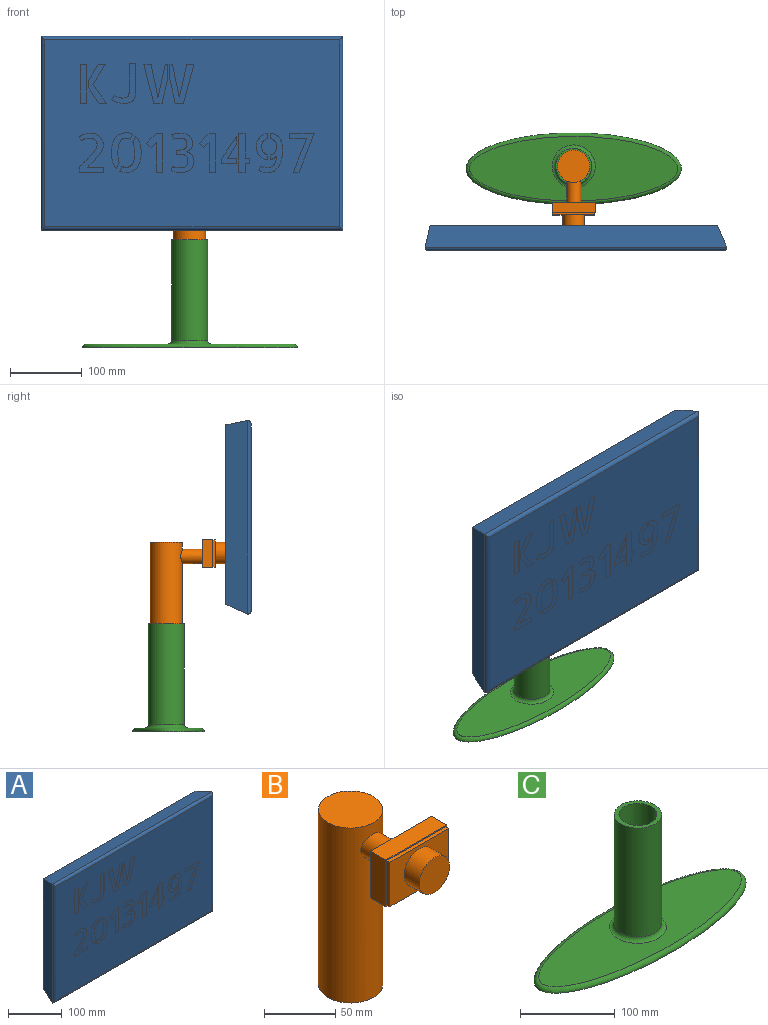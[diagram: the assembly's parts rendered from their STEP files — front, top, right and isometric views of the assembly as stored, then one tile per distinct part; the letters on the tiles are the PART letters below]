
ASSEMBLY  parts=3 mates=3
PART A: 285 faces, bbox 420x35.1x270 mm
  f0: plane 170x100mm, normal (0,1,0), area 13619.9mm2, adj f11,f12,f13,f14,f15,f16,f17,f18
  f1: plane 410x260mm, normal (0,-1,0), area 97142mm2, adj f7,f8,f9,f10,f33,f34,f35,f36
  f2: plane 400x250mm, normal (0,1,0), area 82293.1mm2, adj f3,f4,f5,f6,f11,f12,f13,f14
  f3: plane 270x30mm, normal (-0.98,0.22,0), area 7998.6mm2, adj f2,f4,f6,f7
  f4: plane 420x30mm, normal (0,0.42,-0.91), area 13536.7mm2, adj f2,f3,f5,f9
  f5: plane 270x30mm, normal (0.92,0.4,0), area 8520.4mm2, adj f2,f4,f6,f10
  f6: plane 420x30mm, normal (0,0.2,0.98), area 12561mm2, adj f2,f3,f5,f8
  f7: cylinder r=5mm len=270mm, axis (0,0,-1), area 2092mm2, adj f1,f3,f8,f9
  f8: cylinder r=5mm len=420mm, axis (-1,0,0), area 3270.1mm2, adj f1,f6,f7,f10
  f9: cylinder r=5mm len=420mm, axis (1,0,0), area 3270.1mm2, adj f1,f4,f7,f10
  f10: cylinder r=5mm len=270mm, axis (0,0,1), area 2092mm2, adj f1,f5,f8,f9
  f11: plane 100x15mm, normal (-1,0,0), area 1500mm2, adj f0,f2,f12,f14
  f12: plane 170x15mm, normal (0,0,1), area 2550mm2, adj f0,f2,f11,f13
  f13: plane 100x15mm, normal (1,0,0), area 1500mm2, adj f0,f2,f12,f14
  f14: plane 170x15mm, normal (0,0,-1), area 2550mm2, adj f0,f2,f11,f13
  f15: plane 15x10mm, normal (-1,0,0), area 150mm2, adj f0,f16,f18,f19
  f16: plane 30x10mm, normal (0,0,1), area 300mm2, adj f0,f15,f17,f19
  f17: plane 15x10mm, normal (1,0,0), area 150mm2, adj f0,f16,f18,f19
  f18: plane 30x10mm, normal (0,0,-1), area 300mm2, adj f0,f15,f17,f19
  f19: plane 30x15mm, normal (0,1,0), area 450mm2, adj f15,f16,f17,f18
  f20: plane 60x15mm, normal (0,0,1), area 900mm2, adj f0,f21,f23,f24
  f21: plane 40x15mm, normal (1,0,0), area 600mm2, adj f0,f20,f22,f24
  f22: plane 60x15mm, normal (0,0,-1), area 900mm2, adj f0,f21,f23,f24
  f23: plane 40x15mm, normal (-1,0,0), area 600mm2, adj f0,f20,f22,f24
  f24: plane 60x40mm, normal (0,1,0), area 2400mm2, adj f20,f21,f22,f23
  f25: cylinder r=7.5mm len=15mm, axis (0,1,0), area 706.9mm2, adj f0,f26
  f26: plane 15x15mm, normal (0,1,0), area 176.7mm2, adj f25
  f27: cylinder r=7.5mm len=15mm, axis (0,1,0), area 706.9mm2, adj f0,f28
  f28: plane 15x15mm, normal (0,1,0), area 176.7mm2, adj f27
  f29: cylinder r=7.5mm len=15mm, axis (0,1,0), area 706.9mm2, adj f0,f30
  f30: plane 15x15mm, normal (0,1,0), area 176.7mm2, adj f29
  f31: cylinder r=15mm len=30mm, axis (0,1,0), area 942.5mm2, adj f2,f32
  f32: plane 30x30mm, normal (0,1,0), area 706.9mm2, adj f31
  f33: plane 8.95x0.1mm, normal (0,0,-1), area 0.9mm2, adj f1,f34,f36,f37
  f34: plane 54.03x0.1mm, normal (1,0,0), area 5.4mm2, adj f1,f33,f35,f37
  f35: plane 8.95x0.1mm, normal (0,0,1), area 0.9mm2, adj f1,f34,f36,f37
  f36: plane 54.03x0.1mm, normal (-1,0,0), area 5.4mm2, adj f1,f33,f35,f37
  f37: plane 54.03x8.95mm, normal (0,-1,0), area 483.5mm2, adj f33,f34,f35,f36
  f38: plane 27.78x17.3mm, normal (0.85,0,-0.53), area 3.3mm2, adj f1,f39,f44,f45
  f39: plane 10.04x0.1mm, normal (0,0,1), area 1mm2, adj f1,f38,f40,f45
  f40: plane 22.06x13.13mm, normal (-0.86,0,0.51), area 2.6mm2, adj f1,f39,f41,f45
  f41: plane 10.7x0.1mm, normal (-1,0,0), area 1.1mm2, adj f1,f40,f42,f45
  f42: plane 21.27x14.44mm, normal (-0.83,0,-0.56), area 2.6mm2, adj f1,f41,f43,f45
  f43: plane 10.19x0.1mm, normal (0,0,-1), area 1mm2, adj f1,f42,f44,f45
  f44: plane 26.25x18.77mm, normal (0.81,0,0.58), area 3.2mm2, adj f1,f38,f43,f45
  f45: plane 54.03x24.63mm, normal (0,-1,0), area 505.1mm2, adj f38,f39,f40,f41,f42,f43,f44
  f46: plane 8.94x0.1mm, normal (0,0,1), area 0.9mm2, adj f1,f47,f63,f64
  f47: plane 41.35x0.1mm, normal (-1,0,0), area 4.1mm2, adj f1,f46,f48,f64
  f48: extruded ~5.09x2.46mm, area 0.6mm2, adj f1,f47,f49,f64
  f49: extruded ~6.2x1.5mm, area 0.6mm2, adj f1,f48,f50,f64
  f50: extruded ~3.3x0.36mm, area 0.3mm2, adj f1,f49,f51,f64
  f51: extruded ~3.37x0.84mm, area 0.3mm2, adj f1,f50,f52,f64
  f52: extruded ~2.97x1.03mm, area 0.3mm2, adj f1,f51,f53,f64
  f53: extruded ~2.09x1.07mm, area 0.2mm2, adj f1,f52,f54,f64
  f54: plane 5.94x3.73mm, normal (-0.85,0,0.53), area 0.7mm2, adj f1,f53,f55,f64
  f55: extruded ~3.59x1.98mm, area 0.4mm2, adj f1,f54,f56,f64
  f56: extruded ~4.43x1.58mm, area 0.5mm2, adj f1,f55,f57,f64
  f57: extruded ~4.47x1.03mm, area 0.5mm2, adj f1,f56,f58,f64
  f58: extruded ~3.77x0.33mm, area 0.4mm2, adj f1,f57,f59,f64
  f59: extruded ~6.27x0.62mm, area 0.6mm2, adj f1,f58,f60,f64
  f60: extruded ~5.39x2.2mm, area 0.6mm2, adj f1,f59,f61,f64
  f61: extruded ~4.18x3.74mm, area 0.6mm2, adj f1,f60,f62,f64
  f62: extruded ~6.42x1.39mm, area 0.7mm2, adj f1,f61,f63,f64
  f63: plane 42.07x0.1mm, normal (1,0,0), area 4.2mm2, adj f1,f46,f62,f64
  f64: plane 55.49x33.05mm, normal (0,-1,0), area 637.1mm2, adj f46,f47,f48,f49,f50,f51,f52,f53
  f65: plane 46.62x9.54mm, normal (0.98,0,0.2), area 4.8mm2, adj f1,f66,f72,f73
  f66: plane 9.97x0.1mm, normal (0,0,1), area 1mm2, adj f1,f65,f67,f73
  f67: plane 54.32x13.71mm, normal (-0.97,0,-0.24), area 5.6mm2, adj f1,f66,f68,f73
  f68: plane 11.51x0.1mm, normal (0,0,-1), area 1.2mm2, adj f1,f67,f69,f73
  f69: plane 34.75x8mm, normal (0.97,0,-0.22), area 3.6mm2, adj f1,f68,f70,f73
  f70: plane 19.56x0.1mm, normal (1,0,0), area 2mm2, adj f1,f69,f71,f73
  f71: plane 3.45x0.1mm, normal (0,0,1), area 0.3mm2, adj f1,f70,f72,f73
  f72: plane 46.62x10.26mm, normal (-0.98,0,0.21), area 4.8mm2, adj f1,f65,f71,f73
  f73: plane 54.32x33.22mm, normal (0,-1,0), area 831.4mm2, adj f65,f66,f67,f68,f69,f70,f71,f72
  f74: plane 46.62x10.35mm, normal (-0.98,0,0.22), area 4.8mm2, adj f1,f75,f81,f82
  f75: plane 46.62x9.52mm, normal (0.98,0,0.2), area 4.8mm2, adj f1,f74,f76,f82
  f76: plane 3.52x0.1mm, normal (0,0,1), area 0.4mm2, adj f1,f75,f77,f82
  f77: plane 20.96x0.1mm, normal (-1,0,0), area 2.1mm2, adj f1,f76,f78,f82
  f78: plane 33.36x7.33mm, normal (-0.98,0,-0.21), area 3.4mm2, adj f1,f77,f79,f82
  f79: plane 11.44x0.1mm, normal (0,0,-1), area 1.1mm2, adj f1,f78,f80,f82
  f80: plane 54.32x14.59mm, normal (0.97,0,-0.26), area 5.6mm2, adj f1,f79,f81,f82
  f81: plane 9.97x0.1mm, normal (0,0,1), area 1mm2, adj f1,f74,f80,f82
  f82: plane 54.32x33.36mm, normal (0,-1,0), area 830.2mm2, adj f74,f75,f76,f77,f78,f79,f80,f81
  f83: extruded ~5.64x1.07mm, area 0.6mm2, adj f1,f84,f115,f116
  f84: extruded ~5.31x3.27mm, area 0.6mm2, adj f1,f83,f85,f116
  f85: extruded ~5.61x3.92mm, area 0.7mm2, adj f1,f84,f86,f116
  f86: extruded ~8.17x1.54mm, area 0.8mm2, adj f1,f85,f87,f116
  f87: extruded ~3.81x0.33mm, area 0.4mm2, adj f1,f86,f88,f116
  f88: extruded ~4.14x0.92mm, area 0.4mm2, adj f1,f87,f89,f116
  f89: extruded ~4.04x1.54mm, area 0.4mm2, adj f1,f88,f90,f116
  f90: extruded ~3.26x2.12mm, area 0.4mm2, adj f1,f89,f91,f116
  f91: plane 5.43x2.57mm, normal (-0.9,0,-0.43), area 0.6mm2, adj f1,f90,f92,f116
  f92: extruded ~2.34x1.33mm, area 0.3mm2, adj f1,f91,f93,f116
  f93: extruded ~2.49x0.92mm, area 0.3mm2, adj f1,f92,f94,f116
  f94: extruded ~3.27x0.51mm, area 0.3mm2, adj f1,f93,f95,f116
  f95: extruded ~4.72x0.18mm, area 0.5mm2, adj f1,f94,f96,f116
  f96: extruded ~3.12x0.44mm, area 0.3mm2, adj f1,f95,f97,f116
  f97: extruded ~3.04x1.54mm, area 0.3mm2, adj f1,f96,f98,f116
  f98: extruded ~2.82x2.31mm, area 0.4mm2, adj f1,f97,f99,f116
  f99: extruded ~4.29x0.92mm, area 0.4mm2, adj f1,f98,f100,f116
  f100: extruded ~5.27x1.43mm, area 0.6mm2, adj f1,f99,f101,f116
  f101: extruded ~5.68x3.67mm, area 0.7mm2, adj f1,f100,f102,f116
  f102: extruded ~5.72x4.95mm, area 0.8mm2, adj f1,f101,f103,f116
  f103: extruded ~5.42x5.31mm, area 0.8mm2, adj f1,f102,f104,f116
  f104: extruded ~5.06x4.51mm, area 0.7mm2, adj f1,f103,f105,f116
  f105: extruded ~3.66x3.19mm, area 0.5mm2, adj f1,f104,f106,f116
  f106: plane 8.21x0.1mm, normal (-1,0,0), area 0.8mm2, adj f1,f105,f107,f116
  f107: plane 33.57x0.1mm, normal (0,0,-1), area 3.4mm2, adj f1,f106,f108,f116
  f108: plane 7.11x0.1mm, normal (1,0,0), area 0.7mm2, adj f1,f107,f109,f116
  f109: plane 22.94x0.1mm, normal (0,0,1), area 2.3mm2, adj f1,f108,f110,f116
  f110: extruded ~3.56x3.41mm, area 0.5mm2, adj f1,f109,f111,f116
  f111: extruded ~4.62x4.51mm, area 0.6mm2, adj f1,f110,f112,f116
  f112: extruded ~5.28x4.91mm, area 0.7mm2, adj f1,f111,f113,f116
  f113: extruded ~5.75x4.51mm, area 0.7mm2, adj f1,f112,f114,f116
  f114: extruded ~6.01x3.3mm, area 0.7mm2, adj f1,f113,f115,f116
  f115: extruded ~5.91x1.25mm, area 0.6mm2, adj f1,f83,f114,f116
  f116: plane 54.4x34.16mm, normal (0,-1,0), area 819.2mm2, adj f83,f84,f85,f86,f87,f88,f89,f90
  f117: extruded ~5.42x1.55mm, area 0.6mm2, adj f1,f118,f132,f133
  f118: plane 6.9x3.23mm, normal (0.91,0,-0.42), area 0.8mm2, adj f1,f117,f119,f133
  f119: extruded ~8.87x1.9mm, area 0.9mm2, adj f1,f118,f120,f133
  f120: extruded ~8.61x1.79mm, area 0.9mm2, adj f1,f119,f121,f133
  f121: extruded ~6.53x5.24mm, area 0.8mm2, adj f1,f120,f122,f133
  f122: extruded ~8.62x4.11mm, area 1mm2, adj f1,f121,f123,f133
  f123: extruded ~11.99x1.43mm, area 1.2mm2, adj f1,f122,f124,f133
  f124: extruded ~13.38x1.83mm, area 1.4mm2, adj f1,f123,f125,f133
  f125: extruded ~8.98x5.21mm, area 1mm2, adj f1,f124,f126,f133
  f126: plane 8.57x4.02mm, normal (0.91,0,-0.42), area 0.9mm2, adj f1,f125,f127,f133
  f127: extruded ~5.86x1.54mm, area 0.6mm2, adj f1,f126,f128,f133
  f128: extruded ~7.92x0.59mm, area 0.8mm2, adj f1,f127,f129,f133
  f129: extruded ~9.53x0.92mm, area 1mm2, adj f1,f128,f130,f133
  f130: extruded ~6.35x2.39mm, area 0.7mm2, adj f1,f129,f131,f133
  f131: extruded ~3.74x3.48mm, area 0.5mm2, adj f1,f130,f132,f133
  f132: extruded ~4.91x1.03mm, area 0.5mm2, adj f1,f117,f131,f133
  f133: plane 49.99x29.53mm, normal (0,-1,0), area 492.5mm2, adj f117,f118,f119,f120,f121,f122,f123,f124
  f134: plane 8.5x4.04mm, normal (-0.9,0,0.43), area 0.9mm2, adj f1,f135,f150,f151
  f135: extruded ~0.14x0.1mm, area 0mm2, adj f1,f134,f136,f151
  f136: extruded ~5.87x1.69mm, area 0.6mm2, adj f1,f135,f137,f151
  f137: extruded ~8.06x0.66mm, area 0.8mm2, adj f1,f136,f138,f151
  f138: extruded ~9.57x0.92mm, area 1mm2, adj f1,f137,f139,f151
  f139: extruded ~6.34x2.38mm, area 0.7mm2, adj f1,f138,f140,f151
  f140: extruded ~3.77x3.48mm, area 0.5mm2, adj f1,f139,f141,f151
  f141: extruded ~4.96x1.07mm, area 0.5mm2, adj f1,f140,f142,f151
  f142: extruded ~5.71x1.84mm, area 0.6mm2, adj f1,f141,f143,f151
  f143: plane 6.97x3.3mm, normal (-0.9,0,0.43), area 0.8mm2, adj f1,f142,f144,f151
  f144: extruded ~9.23x2.05mm, area 1mm2, adj f1,f143,f145,f151
  f145: extruded ~8.66x1.76mm, area 0.9mm2, adj f1,f144,f146,f151
  f146: extruded ~6.52x5.2mm, area 0.8mm2, adj f1,f145,f147,f151
  f147: extruded ~8.65x4.14mm, area 1mm2, adj f1,f146,f148,f151
  f148: extruded ~12.02x1.43mm, area 1.2mm2, adj f1,f147,f149,f151
  f149: extruded ~13.57x1.87mm, area 1.4mm2, adj f1,f148,f150,f151
  f150: extruded ~9.01x5.46mm, area 1.1mm2, adj f1,f134,f149,f151
  f151: plane 50.21x29.98mm, normal (0,-1,0), area 500.3mm2, adj f134,f135,f136,f137,f138,f139,f140,f141
  f152: plane 54.03x0.1mm, normal (1,0,0), area 5.4mm2, adj f1,f153,f158,f159
  f153: plane 8.95x0.1mm, normal (0,0,1), area 0.9mm2, adj f1,f152,f154,f159
  f154: plane 13.71x13.7mm, normal (-0.71,0,0.71), area 1.9mm2, adj f1,f153,f155,f159
  f155: plane 6.31x6.31mm, normal (-0.71,0,-0.71), area 0.9mm2, adj f1,f154,f156,f159
  f156: plane 7.4x7.4mm, normal (0.71,0,-0.71), area 1mm2, adj f1,f155,f157,f159
  f157: plane 41.42x0.1mm, normal (-1,0,0), area 4.1mm2, adj f1,f156,f158,f159
  f158: plane 8.95x0.1mm, normal (0,0,-1), area 0.9mm2, adj f1,f152,f157,f159
  f159: plane 54.03x22.66mm, normal (0,-1,0), area 616.6mm2, adj f152,f153,f154,f155,f156,f157,f158
  f160: plane 5.95x0.1mm, normal (-1,0,-0.01), area 0.6mm2, adj f1,f161,f204,f205
  f161: plane 7.4x0.1mm, normal (0,0,-1), area 0.7mm2, adj f1,f160,f162,f205
  f162: extruded ~6.67x2.71mm, area 0.7mm2, adj f1,f161,f163,f205
  f163: extruded ~6.67x2.28mm, area 0.7mm2, adj f1,f162,f164,f205
  f164: extruded ~6.93x2.49mm, area 0.8mm2, adj f1,f163,f165,f205
  f165: extruded ~7.56x2.75mm, area 0.8mm2, adj f1,f164,f166,f205
  f166: extruded ~5.42x0.26mm, area 0.5mm2, adj f1,f165,f167,f205
  f167: extruded ~3.08x0.66mm, area 0.3mm2, adj f1,f166,f168,f205
  f168: extruded ~1.68x0.84mm, area 0.2mm2, adj f1,f167,f169,f205
  f169: extruded ~1.26x0.8mm, area 0.1mm2, adj f1,f168,f170,f205
  f170: plane 6.3x1.97mm, normal (-0.95,0,0.3), area 0.7mm2, adj f1,f169,f171,f205
  f171: extruded ~4.94x1.72mm, area 0.5mm2, adj f1,f170,f172,f205
  f172: extruded ~9.72x0.84mm, area 1mm2, adj f1,f171,f173,f205
  f173: extruded ~2.45x0.15mm, area 0.2mm2, adj f1,f172,f174,f205
  f174: extruded ~3.48x0.66mm, area 0.4mm2, adj f1,f173,f175,f205
  f175: extruded ~3.92x1.58mm, area 0.4mm2, adj f1,f174,f176,f205
  f176: extruded ~3.63x2.83mm, area 0.5mm2, adj f1,f175,f177,f205
  f177: extruded ~4.43x2.67mm, area 0.5mm2, adj f1,f176,f178,f205
  f178: extruded ~6.33x1.06mm, area 0.6mm2, adj f1,f177,f179,f205
  f179: extruded ~5.32x1.03mm, area 0.5mm2, adj f1,f178,f180,f205
  f180: extruded ~3.92x2.56mm, area 0.5mm2, adj f1,f179,f181,f205
  f181: extruded ~3.33x2.49mm, area 0.4mm2, adj f1,f180,f182,f205
  f182: extruded ~3.48x1.1mm, area 0.4mm2, adj f1,f181,f183,f205
  f183: extruded ~2.86x1.21mm, area 0.3mm2, adj f1,f182,f184,f205
  f184: extruded ~2.79x2.31mm, area 0.4mm2, adj f1,f183,f185,f205
  f185: extruded ~3.27x2.05mm, area 0.4mm2, adj f1,f184,f186,f205
  f186: extruded ~4.13x0.81mm, area 0.4mm2, adj f1,f185,f187,f205
  f187: extruded ~6.75x1.35mm, area 0.7mm2, adj f1,f186,f188,f205
  f188: extruded ~4.69x3.67mm, area 0.6mm2, adj f1,f187,f189,f205
  f189: extruded ~5.39x2.67mm, area 0.6mm2, adj f1,f188,f190,f205
  f190: extruded ~6.53x0.84mm, area 0.7mm2, adj f1,f189,f191,f205
  f191: extruded ~7.51x0.59mm, area 0.8mm2, adj f1,f190,f192,f205
  f192: extruded ~4.36x1.09mm, area 0.4mm2, adj f1,f191,f193,f205
  f193: plane 6.6x2.56mm, normal (-0.93,0,-0.36), area 0.7mm2, adj f1,f192,f194,f205
  f194: extruded ~3.05x0.99mm, area 0.3mm2, adj f1,f193,f195,f205
  f195: extruded ~5.38x0.63mm, area 0.5mm2, adj f1,f194,f196,f205
  f196: extruded ~5.28x0.77mm, area 0.5mm2, adj f1,f195,f197,f205
  f197: extruded ~2.89x2.02mm, area 0.4mm2, adj f1,f196,f198,f205
  f198: extruded ~2.71x1.21mm, area 0.3mm2, adj f1,f197,f199,f205
  f199: extruded ~2.79x0.22mm, area 0.3mm2, adj f1,f198,f200,f205
  f200: extruded ~5.06x0.96mm, area 0.5mm2, adj f1,f199,f201,f205
  f201: extruded ~2.49x2.42mm, area 0.4mm2, adj f1,f200,f202,f205
  f202: extruded ~3.11x0.8mm, area 0.3mm2, adj f1,f201,f203,f205
  f203: extruded ~3.26x0.1mm, area 0.3mm2, adj f1,f202,f204,f205
  f204: plane 4.99x0.1mm, normal (0,0,1), area 0.5mm2, adj f1,f160,f203,f205
  f205: plane 54.68x31.88mm, normal (0,-1,0), area 724mm2, adj f160,f161,f162,f163,f164,f165,f166,f167
  f206: plane 54.03x0.1mm, normal (1,0,0), area 5.4mm2, adj f1,f207,f212,f213
  f207: plane 8.95x0.1mm, normal (0,0,1), area 0.9mm2, adj f1,f206,f208,f213
  f208: plane 13.71x13.7mm, normal (-0.71,0,0.71), area 1.9mm2, adj f1,f207,f209,f213
  f209: plane 6.31x6.31mm, normal (-0.71,0,-0.71), area 0.9mm2, adj f1,f208,f210,f213
  f210: plane 7.4x7.4mm, normal (0.71,0,-0.71), area 1mm2, adj f1,f209,f211,f213
  f211: plane 41.42x0.1mm, normal (-1,0,0), area 4.1mm2, adj f1,f210,f212,f213
  f212: plane 8.95x0.1mm, normal (0,0,-1), area 0.9mm2, adj f1,f206,f211,f213
  f213: plane 54.03x22.66mm, normal (0,-1,0), area 616.6mm2, adj f206,f207,f208,f209,f210,f211,f212
  f214: plane 34.45x0.1mm, normal (1,0,0), area 3.4mm2, adj f1,f215,f221,f222
  f215: plane 8.95x0.1mm, normal (0,0,1), area 0.9mm2, adj f1,f214,f216,f222
  f216: plane 54.03x0.1mm, normal (-1,0,0), area 5.4mm2, adj f1,f215,f217,f222
  f217: plane 8.95x0.1mm, normal (0,0,-1), area 0.9mm2, adj f1,f216,f218,f222
  f218: plane 12.61x0.1mm, normal (1,0,0), area 1.3mm2, adj f1,f217,f219,f222
  f219: plane 5.64x0.1mm, normal (0,0,-1), area 0.6mm2, adj f1,f218,f220,f222
  f220: plane 6.97x0.1mm, normal (1,0,0), area 0.7mm2, adj f1,f219,f221,f222
  f221: plane 5.64x0.1mm, normal (0,0,1), area 0.6mm2, adj f1,f214,f220,f222
  f222: plane 54.03x14.59mm, normal (0,-1,0), area 522.8mm2, adj f214,f215,f216,f217,f218,f219,f220,f221
  f223: plane 20.37x0.1mm, normal (0,0,-1), area 2mm2, adj f1,f224,f229,f230
  f224: plane 6.97x0.1mm, normal (1,0,0), area 0.7mm2, adj f1,f223,f225,f230
  f225: plane 12.54x0.1mm, normal (0,0,1), area 1.3mm2, adj f1,f224,f226,f230
  f226: plane 19.58x12.54mm, normal (0.84,0,-0.54), area 2.3mm2, adj f1,f225,f227,f230
  f227: plane 10.47x0.1mm, normal (1,0,0), area 1mm2, adj f1,f226,f228,f230
  f228: plane 30.05x20.37mm, normal (-0.83,0,0.56), area 3.6mm2, adj f1,f227,f229,f230
  f229: plane 6.97x0.1mm, normal (-1,0,0), area 0.7mm2, adj f1,f223,f228,f230
  f230: plane 37.02x20.37mm, normal (0,-1,0), area 325.3mm2, adj f223,f224,f225,f226,f227,f228,f229
  f231: plane 6.66x0.1mm, normal (1,0,0), area 0.7mm2, adj f1,f232,f244,f245
  f232: extruded ~6.12x3.67mm, area 0.7mm2, adj f1,f231,f233,f245
  f233: extruded ~7.63x2.38mm, area 0.8mm2, adj f1,f232,f234,f245
  f234: extruded ~7.81x2.38mm, area 0.8mm2, adj f1,f233,f235,f245
  f235: extruded ~6.12x3.92mm, area 0.7mm2, adj f1,f234,f236,f245
  f236: plane 7.11x0.1mm, normal (1,0,0), area 0.7mm2, adj f1,f235,f237,f245
  f237: extruded ~5.5x1.35mm, area 0.6mm2, adj f1,f236,f238,f245
  f238: extruded ~5.21x3.44mm, area 0.6mm2, adj f1,f237,f239,f245
  f239: extruded ~5.94x3.92mm, area 0.7mm2, adj f1,f238,f240,f245
  f240: extruded ~8.84x1.57mm, area 0.9mm2, adj f1,f239,f241,f245
  f241: extruded ~6.05x1.1mm, area 0.6mm2, adj f1,f240,f242,f245
  f242: extruded ~5.46x3.23mm, area 0.6mm2, adj f1,f241,f243,f245
  f243: extruded ~5.13x4.03mm, area 0.7mm2, adj f1,f242,f244,f245
  f244: extruded ~6.74x1.68mm, area 0.7mm2, adj f1,f231,f243,f245
  f245: plane 36.79x16.2mm, normal (0,-1,0), area 316.5mm2, adj f231,f232,f233,f234,f235,f236,f237,f238
  f246: plane 7.19x0.1mm, normal (-1,0,0), area 0.7mm2, adj f1,f247,f276,f277
  f247: extruded ~3.71x1.21mm, area 0.4mm2, adj f1,f246,f248,f277
  f248: extruded ~2.93x2.53mm, area 0.4mm2, adj f1,f247,f249,f277
  f249: extruded ~3.6x1.94mm, area 0.4mm2, adj f1,f248,f250,f277
  f250: extruded ~4.47x0.73mm, area 0.5mm2, adj f1,f249,f251,f277
  f251: extruded ~4.36x0.73mm, area 0.4mm2, adj f1,f250,f252,f277
  f252: extruded ~3.48x1.94mm, area 0.4mm2, adj f1,f251,f253,f277
  f253: extruded ~2.9x2.38mm, area 0.4mm2, adj f1,f252,f254,f277
  f254: extruded ~3.74x1.14mm, area 0.4mm2, adj f1,f253,f255,f277
  f255: plane 6.45x0.1mm, normal (-1,0,0), area 0.6mm2, adj f1,f254,f256,f277
  f256: extruded ~5.32x1.61mm, area 0.6mm2, adj f1,f255,f257,f277
  f257: extruded ~3.04x2.86mm, area 0.4mm2, adj f1,f256,f258,f277
  f258: extruded ~0.29x0.1mm, area 0mm2, adj f1,f257,f259,f277
  f259: extruded ~0.3x0.1mm, area 0mm2, adj f1,f258,f260,f277
  f260: extruded ~5.91x0.73mm, area 0.6mm2, adj f1,f259,f261,f277
  f261: extruded ~4.99x2.16mm, area 0.5mm2, adj f1,f260,f262,f277
  f262: extruded ~3.63x3.48mm, area 0.5mm2, adj f1,f261,f263,f277
  f263: extruded ~5.2x1.32mm, area 0.5mm2, adj f1,f262,f264,f277
  f264: extruded ~5.76x0.37mm, area 0.6mm2, adj f1,f263,f265,f277
  f265: extruded ~4.5x1.68mm, area 0.5mm2, adj f1,f264,f266,f277
  f266: plane 6.08x2.86mm, normal (-0.9,0,0.43), area 0.7mm2, adj f1,f265,f267,f277
  f267: extruded ~6.23x2.31mm, area 0.7mm2, adj f1,f266,f268,f277
  f268: extruded ~7.69x0.55mm, area 0.8mm2, adj f1,f267,f269,f277
  f269: extruded ~6.93x1.5mm, area 0.7mm2, adj f1,f268,f270,f277
  f270: extruded ~6.3x5.28mm, area 0.8mm2, adj f1,f269,f271,f277
  f271: extruded ~10.15x4.58mm, area 1.1mm2, adj f1,f270,f272,f277
  f272: extruded ~16.05x1.76mm, area 1.6mm2, adj f1,f271,f273,f277
  f273: extruded ~8.51x1.03mm, area 0.9mm2, adj f1,f272,f274,f277
  f274: extruded ~6.78x3.26mm, area 0.8mm2, adj f1,f273,f275,f277
  f275: extruded ~5.54x4.58mm, area 0.7mm2, adj f1,f274,f276,f277
  f276: extruded ~7.77x1.91mm, area 0.8mm2, adj f1,f246,f275,f277
  f277: plane 54.76x33.5mm, normal (0,-1,0), area 632.2mm2, adj f246,f247,f248,f249,f250,f251,f252,f253
  f278: plane 8.21x0.1mm, normal (0,0,-1), area 0.8mm2, adj f1,f279,f283,f284
  f279: plane 54.03x20.97mm, normal (0.93,0,-0.36), area 5.8mm2, adj f1,f278,f280,f284
  f280: plane 33.94x0.1mm, normal (0,0,1), area 3.4mm2, adj f1,f279,f281,f284
  f281: plane 7.18x0.1mm, normal (-1,0,0), area 0.7mm2, adj f1,f280,f282,f284
  f282: plane 23.53x0.1mm, normal (0,0,-1), area 2.4mm2, adj f1,f281,f283,f284
  f283: plane 46.85x18.77mm, normal (-0.93,0,0.37), area 5mm2, adj f1,f278,f282,f284
  f284: plane 54.03x33.94mm, normal (0,-1,0), area 604.7mm2, adj f278,f279,f280,f281,f282,f283
PART B: 17 faces, bbox 60x105.5x154.2 mm
  f0: cylinder r=10mm len=29.84mm, axis (0,1,0), area 1800.7mm2, adj f6,f7
  f1: plane 60x15mm, normal (0,0,1), area 900mm2, adj f2,f4,f5,f6
  f2: plane 40x15mm, normal (-1,0,0), area 600mm2, adj f1,f3,f5,f6
  f3: plane 60x15mm, normal (0,0,-1), area 900mm2, adj f2,f4,f5,f6
  f4: plane 40x15mm, normal (1,0,0), area 600mm2, adj f1,f3,f5,f6
  f5: plane 60x40mm, normal (0,-1,0), area 196mm2, adj f1,f2,f3,f4,f10,f11,f12,f13
  f6: plane 60x40mm, normal (0,1,0), area 2085.8mm2, adj f0,f1,f2,f3,f4
  f7: cylinder r=22.5mm len=150mm, axis (0,0,1), area 20882.9mm2, adj f0,f8,f9
  f8: plane 45x45mm, normal (0,0,-1), area 1590.4mm2, adj f7
  f9: plane 45x45mm, normal (0,0,1), area 1590.4mm2, adj f7
  f10: plane 38x3mm, normal (-1,0,0), area 114mm2, adj f5,f11,f13,f14
  f11: plane 58x3mm, normal (0,0,-1), area 174mm2, adj f5,f10,f12,f14
  f12: plane 38x3mm, normal (1,0,0), area 114mm2, adj f5,f11,f13,f14
  f13: plane 58x3mm, normal (0,0,1), area 174mm2, adj f5,f10,f12,f14
  f14: plane 58x38mm, normal (0,-1,0), area 1497.1mm2, adj f10,f11,f12,f13,f15
  f15: cylinder r=15mm len=30mm, axis (0,1,0), area 1413.7mm2, adj f14,f16
  f16: plane 30x30mm, normal (0,-1,0), area 706.9mm2, adj f15
PART C: 8 faces, bbox 300.2x100.2x150.5 mm
  f0: cylinder r=20mm len=145.31mm, axis (0,0,1), area 18260.6mm2, adj f1,f4
  f1: plane 50x50mm, normal (0,0,1), area 706.9mm2, adj f0,f2
  f2: cylinder r=25mm len=140.31mm, axis (0,0,1), area 22040.4mm2, adj f1,f6
  f3: plane 290.01x90.01mm, normal (0,0,1), area 17472.1mm2, adj f6,f7
  f4: plane 40x40mm, normal (0,0,1), area 1256.6mm2, adj f0
  f5: plane 300.22x100.22mm, normal (0,0,-1), area 23561.9mm2, adj f7
  f6: torus R=30mm, axis (0,0,1), area 1323.4mm2, adj f2,f3
  f7: bspline ~300.01x100.01mm, area 5156.7mm2, adj f3,f5
PLACE A t=(0.91,-363.74,-263.67)mm
PLACE B rot(axis=(0.92,0.3,0.25),0deg) t=(0.91,-280.74,-444.23)mm
PLACE C t=(0.91,-283.85,-557.84)mm
MATE revolute A.f31 <-> B.f15  axis (0,1,0) through (0.91,-363.74,-308.99)mm
MATE parallel A.f2 <-> B.f15  axis (0,1,0) through (-84.09,-363.74,-270.95)mm
MATE slider C.f0 <-> B.f7  axis (0,0,1) through (0.91,-280.74,-407.53)mm
